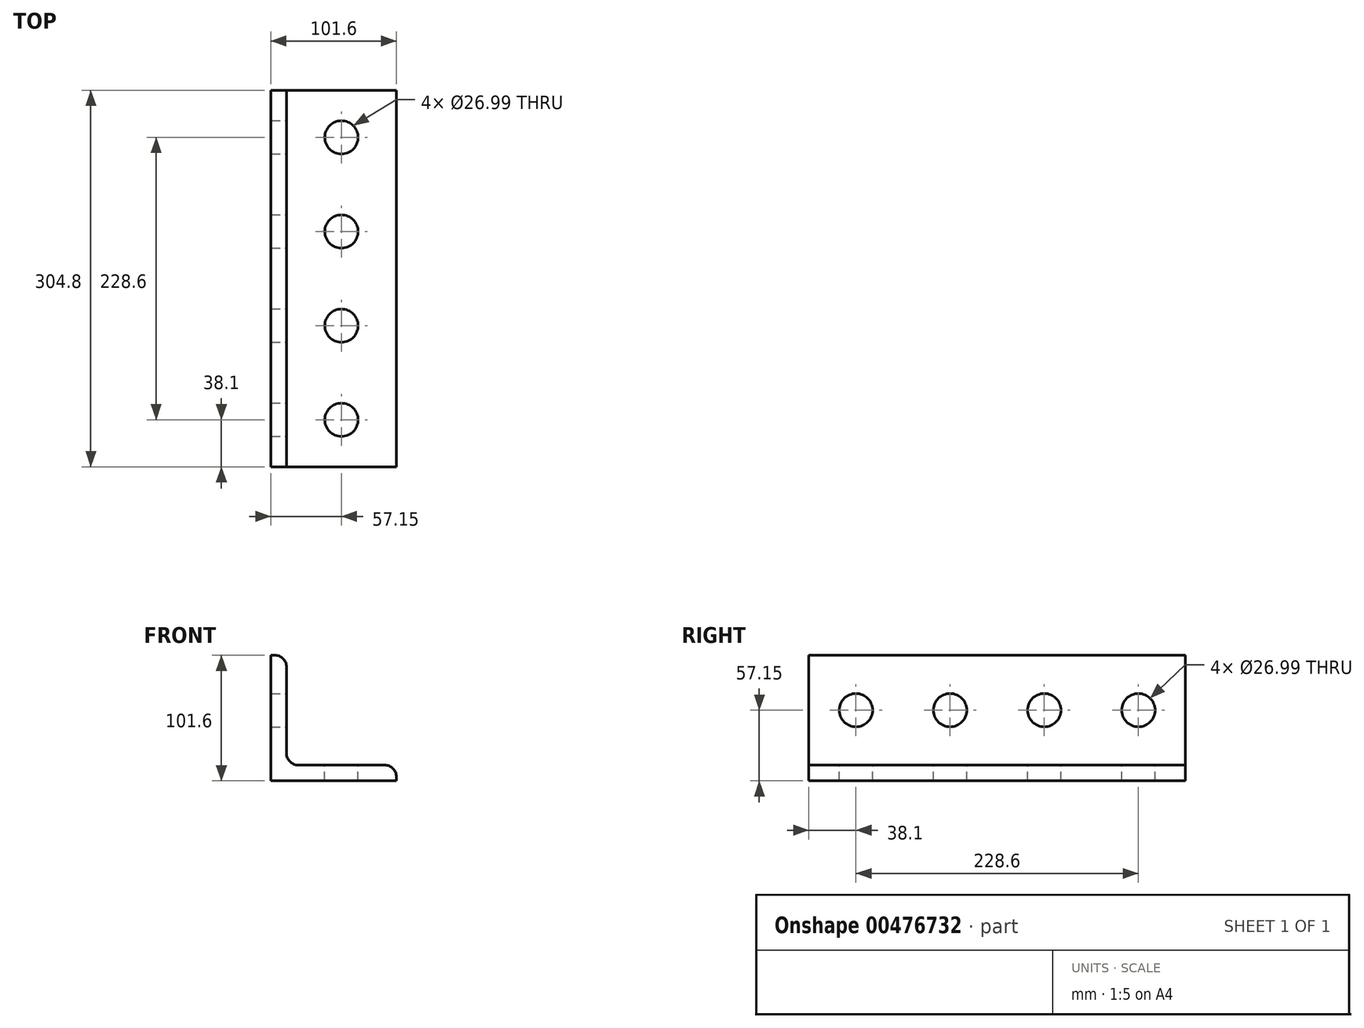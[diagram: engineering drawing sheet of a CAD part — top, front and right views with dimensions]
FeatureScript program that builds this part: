
annotation { "Feature Type Name" : "Feature", "Feature Type Description" : "" }
export const myFeature = defineFeature(function(context is Context, id is Id, definition is map)
    precondition{}
    {
        {
            var Q0;
            Q0=qCreatedBy(makeId("Front.planeOp"),FACE);
            var sketch = newSketch(context, id + "F0", { "sketchPlane" : qUnion([Q0])});
            skLineSegment(sketch, "E0", {"start": v(0, 101.6) * mm, "end": v(0, 0) * mm});
            skLineSegment(sketch, "E1", {"start": v(0, 0) * mm, "end": v(101.6, 0) * mm});
            skLineSegment(sketch, "E2", {"start": v(101.6, 0) * mm, "end": v(101.6, 12.7) * mm});
            skLineSegment(sketch, "E3", {"start": v(101.6, 12.7) * mm, "end": v(12.7, 12.7) * mm});
            skLineSegment(sketch, "E4", {"start": v(12.7, 12.7) * mm, "end": v(12.7, 101.6) * mm});
            skLineSegment(sketch, "E5", {"start": v(12.7, 101.6) * mm, "end": v(0, 101.6) * mm});
            skSolve(sketch);
        }
        {
            var Q0;
            Q0=makeQuery(id+"F0.imprint","IMPRINT",FACE,{"disambiguationData":[TD([[makeQuery(id+"F0.imprint","IMPRINT",EDGE,{"derivedFrom":sQuery(id+"F0.wireOp",EDGE,"E0")}),1.0]])]});
            extrude(context, id + "F1", {"entities" : qUnion([Q0]), "depth" : 304.8 * mm});
        }
        {
            var Q0;
            Q0=makeQuery(id+"F1.opExtrude","SWEPT_FACE",FACE,{"disambiguationData":[OSD([sQuery(id+"F0.wireOp",EDGE,"E4")])]});
            var sketch = newSketch(context, id + "F2", { "sketchPlane" : qUnion([Q0])});
            skPoint(sketch, "E6", {"position": v(-266.7, 57.15) * mm});
            skPoint(sketch, "E7", {"position": v(-190.5, 57.15) * mm});
            skPoint(sketch, "E8", {"position": v(-114.3, 57.15) * mm});
            skPoint(sketch, "E9", {"position": v(-38.1, 57.15) * mm});
            skSolve(sketch);
        }
        {
            var Q0;
            Q0=sQuery(id+"F2.wireOp",VERTEX,"E6");
            var Q1;
            Q1=sQuery(id+"F2.wireOp",VERTEX,"E7");
            var Q2;
            Q2=sQuery(id+"F2.wireOp",VERTEX,"E8");
            var Q3;
            Q3=sQuery(id+"F2.wireOp",VERTEX,"E9");
            var Q4;
            Q4=makeQuery(id+"F1.opExtrude","SWEPT_BODY",BODY,{"disambiguationData":[OSD([sQuery(id+"F0.wireOp",EDGE,"E0"),sQuery(id+"F0.wireOp",EDGE,"E1"),sQuery(id+"F0.wireOp",EDGE,"E2"),sQuery(id+"F0.wireOp",EDGE,"E3"),sQuery(id+"F0.wireOp",EDGE,"E4"),sQuery(id+"F0.wireOp",EDGE,"E5")])]});
            hole(context, id + "F3", {"style" : HoleStyle.SIMPLE, "endStyle" : HoleEndStyle.THROUGH, "holeDiameter" : 26.99 * mm, "isTappedThrough" : true, "tappedDepth" : 12.7 * mm, "tapClearance" : 3, "locations" : qUnion([Q0, Q1, Q2, Q3]), "scope" : qUnion([Q4])});
        }
        {
            var Q0;
            Q0=makeQuery(id+"F1.opExtrude","SWEPT_FACE",FACE,{"disambiguationData":[OSD([sQuery(id+"F0.wireOp",EDGE,"E3")])]});
            var sketch = newSketch(context, id + "F4", { "sketchPlane" : qUnion([Q0])});
            skPoint(sketch, "E10", {"position": v(57.15, -38.1) * mm});
            skPoint(sketch, "E10.positionSnap0", {"position": v(57.15, 0) * mm});
            skPoint(sketch, "E11", {"position": v(57.15, -114.3) * mm});
            skPoint(sketch, "E12", {"position": v(57.15, -190.5) * mm});
            skPoint(sketch, "E13", {"position": v(57.15, -266.7) * mm});
            skSolve(sketch);
        }
        {
            var Q0;
            Q0=sQuery(id+"F4.wireOp",VERTEX,"E10");
            var Q1;
            Q1=sQuery(id+"F4.wireOp",VERTEX,"E11");
            var Q2;
            Q2=sQuery(id+"F4.wireOp",VERTEX,"E12");
            var Q3;
            Q3=sQuery(id+"F4.wireOp",VERTEX,"E13");
            var Q4;
            Q4=makeQuery(id+"F1.opExtrude","SWEPT_BODY",BODY,{"disambiguationData":[OSD([sQuery(id+"F0.wireOp",EDGE,"E0"),sQuery(id+"F0.wireOp",EDGE,"E1"),sQuery(id+"F0.wireOp",EDGE,"E2"),sQuery(id+"F0.wireOp",EDGE,"E3"),sQuery(id+"F0.wireOp",EDGE,"E4"),sQuery(id+"F0.wireOp",EDGE,"E5")])]});
            hole(context, id + "F5", {"style" : HoleStyle.SIMPLE, "endStyle" : HoleEndStyle.THROUGH, "holeDiameter" : 26.99 * mm, "isTappedThrough" : true, "tappedDepth" : 12.7 * mm, "tapClearance" : 3, "locations" : qUnion([Q0, Q1, Q2, Q3]), "scope" : qUnion([Q4])});
        }
        {
            var Q0;
            Q0=makeQuery(id+"F1.opExtrude","SWEPT_EDGE",EDGE,{"disambiguationData":[OSD([sQuery(id+"F0.wireOp",EDGE,"E4"),sQuery(id+"F0.wireOp",EDGE,"E5")])]});
            var Q1;
            Q1=makeQuery(id+"F1.opExtrude","SWEPT_EDGE",EDGE,{"disambiguationData":[OSD([sQuery(id+"F0.wireOp",EDGE,"E3"),sQuery(id+"F0.wireOp",EDGE,"E4")])]});
            var Q2;
            Q2=makeQuery(id+"F1.opExtrude","SWEPT_EDGE",EDGE,{"disambiguationData":[OSD([sQuery(id+"F0.wireOp",EDGE,"E2"),sQuery(id+"F0.wireOp",EDGE,"E3")])]});
            fillet(context, id + "F6", {"entities" : qUnion([Q0, Q1, Q2]), "radius" : 9.52 * mm, "tangentPropagation" : true, "allowEdgeOverflow" : false});
        }
    });
